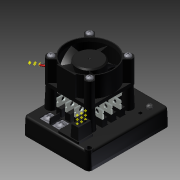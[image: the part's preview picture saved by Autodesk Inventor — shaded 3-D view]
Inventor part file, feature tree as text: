
AUTODESK INVENTOR PART (.ipt)
format: ipt  version: 2013 (Build 170138000, 138)  size: 1,489,408 bytes
history: native  units: in
note: dims shown in document units (in); Inventor stores cm internally (conversion verified against a paired STEP export)
features: other x49, plane x10, sketch x5, extrude x1
ambient origin geometry x8: Origin, YZ Plane, XZ Plane, XY Plane, X Axis, Y Axis, Z Axis, Center Point
bodies: Solid1 (feature_tree)
feature tree (65):
  other  "FR-VIC884.iam"
  other  "FR-VIC884_1.ipt:1"
  other  "FR-VIC884_2.ipt:1"
  other  "KDE1204PKBX-8.iam:1::KDE1204PKBX-8_1.ipt:1"
  other  "KDE1204PKBX-8.iam:1::KDE1204PKBX-8_2.ipt:1"
  other  "KDE1204PKBX-8.iam:1::KDE1204PKBX-8_3.ipt:1"
  other  "KDE1204PKBX-8.iam:1::KDE1204PKBX-8_4.ipt:1"
  other  "FR-VIC884_3.ipt:1"
  other  "FR-VIC884_4.ipt:1"
  other  "FR-VIC884_5.ipt:1"
  other  "FR-VIC884_6.ipt:1"
  other  "FR-VIC884_6.ipt:3"
  other  "FR-VIC884_6.ipt:4"
  other  "FR-VIC884_6.ipt:5"
  other  "FR-VIC884_6.ipt:6"
  other  "FR-VIC884_6.ipt:7"
  other  "FR-VIC884_6.ipt:8"
  other  "FR-VIC884_6.ipt:9"
  other  "FR-VIC884_6.ipt:10"
  other  "FR-VIC884_6.ipt:11"
  other  "FR-VIC884_6.ipt:12"
  other  "FR-VIC884_6.ipt:13"
  other  "FR-VIC884_7.ipt:1"
  other  "FR-VIC884_7.ipt:2"
  other  "FR-VIC884_7.ipt:3"
  other  "FR-VIC884_7.ipt:4"
  other  "Cross Recessed Fillister Head Machine Screw - Type I - Inch No. 4 - 40 - 1:1"
  other  "Cross Recessed Fillister Head Machine Screw - Type I - Inch No. 4 - 40 - 1:2"
  other  "Cross Recessed Fillister Head Machine Screw - Type I - Inch No. 4 - 40 - 1:3"
  other  "Cross Recessed Fillister Head Machine Screw - Type I - Inch No. 4 - 40 - 1:4"
  other  "FR-VIC884.iam_Bodies"
  sketch  "Sketch2"  dims[d0=0.3937in d1=1.0in d2=0.0in]
  sketch  "Sketch3"  dims[d3=0.125in]
  extrude  "Extrusion1"  Depth=1.0in TaperAngle=0.0deg
  other  "Work Point3"
  other  "Work Point4"
  other  "Work Point5"
  other  "Work Point6"
  plane  "Work Plane7"
  other  "Work Point9"
  plane  "Work Plane8"
  other  "Work Point10"
  sketch  "Sketch5"  dims[d5=0.125in]
  other  "Work Point12"
  other  "Work Point13"
  sketch  "Sketch6"  dims[d6=0.25in d7=0.125in d8=0.25in d9=0.125in d10=0.25in d11=0.125in d12=0.25in]
  other  "Work Point15"
  other  "Work Point16"
  sketch  "Sketch4"  dims[d4=0.25in]
  plane  "Work Plane1"
  other  "Work Axis1"
  plane  "Work Plane2"
  other  "Work Axis2"
  plane  "Work Plane3"
  other  "Work Axis3"
  plane  "Work Plane4"
  other  "Work Axis4"
  plane  "Work Plane9"
  other  "Work Axis6"
  plane  "Work Plane10"
  other  "Work Axis7"
  plane  "Work Plane11"
  other  "Work Axis8"
  plane  "Work Plane12"
  other  "Work Axis9"
